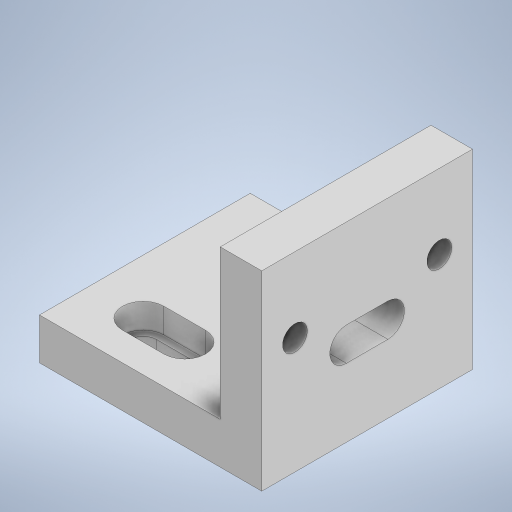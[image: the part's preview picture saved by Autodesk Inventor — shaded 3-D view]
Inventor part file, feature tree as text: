
AUTODESK INVENTOR PART (.ipt)
format: ipt  version: 2024 (Build 280153000, 153)  size: 314,368 bytes
history: native  units: mm
features: extrude x5, sketch x5, projected_geometry x3
ambient origin geometry x8: Origin, YZ Plane, XZ Plane, XY Plane, X Axis, Y Axis, Z Axis, Center Point
bodies: Solid1 (feature_tree)
feature tree (13):
  extrude  "Extrusion1"  Depth=10.0mm
  extrude  "Extrusion2"  Depth=6.35mm
  extrude  "Extrusion3"  Depth=10.0mm
  extrude  "Extrusion4"  Depth=25.4mm
  extrude  "Extrusion5"  Depth=10.0mm
  sketch  "Sketch1"  dims[d0=50.8mm d2=10.0mm]
  sketch  "Sketch2"  dims[d3=6.35mm d4=6.35mm]
  sketch  "Sketch3"  dims[d6=10.0mm d7=20.4mm]
  projected_geometry  "Projected Loop1"
  sketch  "Sketch4"  dims[d8=13.175mm d9=25.4mm]
  projected_geometry  "Projected Loop2"
  sketch  "Sketch5"  dims[d10=10.0mm d11=0.0mm d12=10.0mm d13=36.0mm d14=0.0mm d15=2.84mm d16=2.84mm d17=34.8mm d18=0.0mm d19=18.0mm d20=8.0mm d21=8.0mm d22=50.8mm d23=36.0mm d24=0.0mm d25=10.0mm d26=10.0mm d27=10.0mm d28=10.0mm d29=6.0mm d30=0.0mm d31=6.0mm d32=6.0mm d33=5.0mm d34=0.0mm d35=8.0mm d36=8.0mm d37=0.0mm d38=10.0mm d39=5.0mm d40=25.4mm d41=10.5mm]
  projected_geometry  "Projected Loop3"
